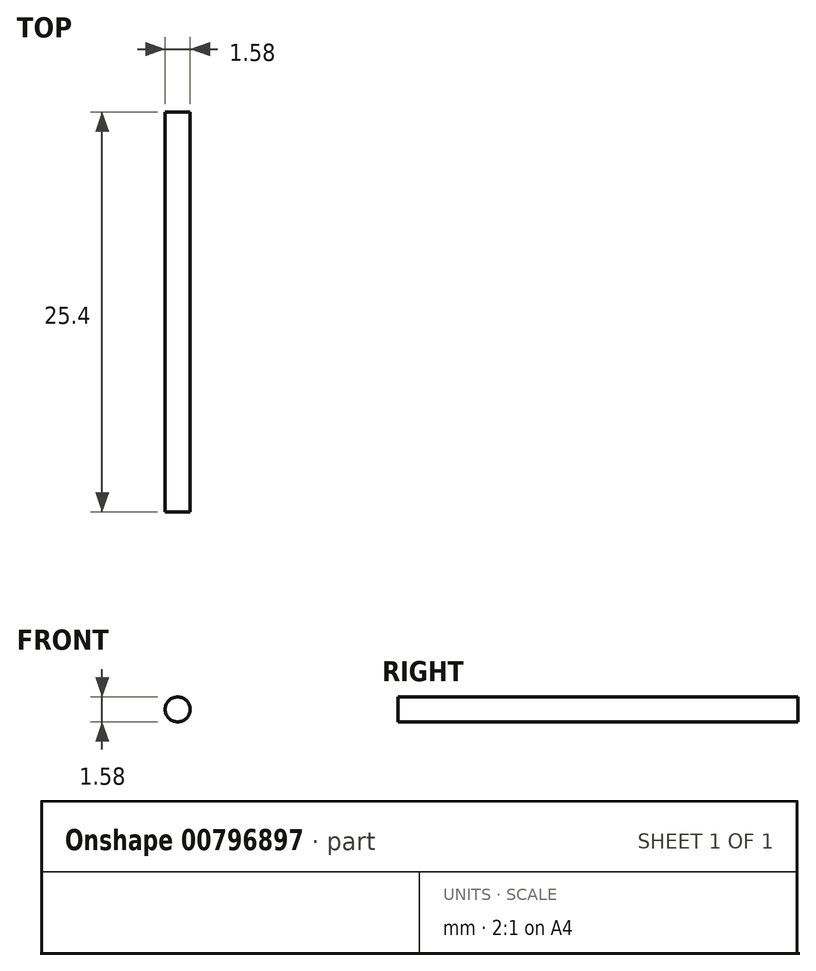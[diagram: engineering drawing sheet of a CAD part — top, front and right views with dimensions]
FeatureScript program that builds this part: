
annotation { "Feature Type Name" : "Feature", "Feature Type Description" : "" }
export const myFeature = defineFeature(function(context is Context, id is Id, definition is map)
    precondition{}
    {
        {
            var Q0;
            Q0=qCreatedBy(makeId("Front.planeOp"),FACE);
            var sketch = newSketch(context, id + "F0", { "sketchPlane" : qUnion([Q0])});
            skCircle(sketch, "E0", {"center": v(0, 0) * mm, "radius": 0.8 * mm});
            skSolve(sketch);
        }
        {
            var Q0;
            Q0 = qSketchRegion(id + "F0", true);
            extrude(context, id + "F1", {"entities" : qUnion([Q0]), "depth" : 25.4 * mm, "offsetDistance" : 25.4 * mm});
        }
    });
